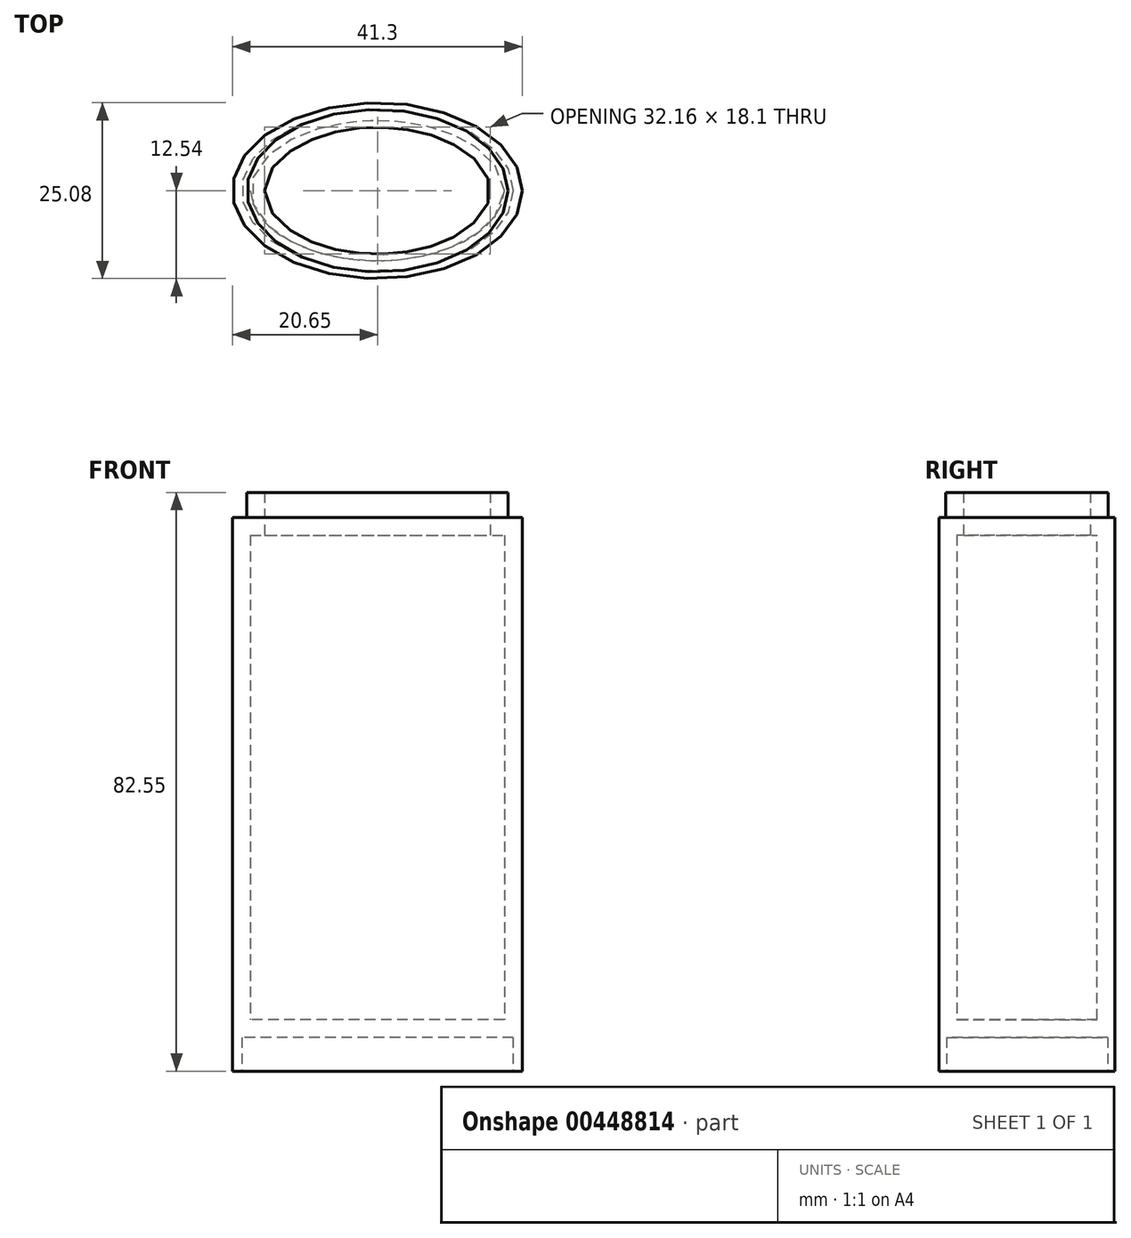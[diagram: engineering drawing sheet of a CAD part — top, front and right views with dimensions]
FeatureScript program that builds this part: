
annotation { "Feature Type Name" : "Feature", "Feature Type Description" : "" }
export const myFeature = defineFeature(function(context is Context, id is Id, definition is map)
    precondition{}
    {
        {
            var Q0;
            Q0=qCreatedBy(makeId("Top.planeOp"),FACE);
            var sketch = newSketch(context, id + "F0", { "sketchPlane" : qUnion([Q0])});
            skEllipse(sketch, "E0", {"center": v(0, 0) * mm, "majorRadius": 20.65 * mm, "minorRadius": 12.54 * mm, "majorAxis": v(1, 0)});
            skSolve(sketch);
        }
        {
            var Q0;
            Q0 = qSketchRegion(id + "F0", true);
            extrude(context, id + "F1", {"entities" : qUnion([Q0]), "depth" : 79 * mm});
        }
        {
            var Q0;
            Q0=makeQuery(id+"F1.opExtrude","CAP_FACE",FACE,{"disambiguationData":[OSD([sQuery(id+"F0.wireOp",EDGE,"E0")])],"isStart":true});
            var sketch = newSketch(context, id + "F2", { "sketchPlane" : qUnion([Q0])});
            skEllipse(sketch, "E1", {"center": v(0, 0) * mm, "majorRadius": 19.36 * mm, "minorRadius": 11.49 * mm, "majorAxis": v(1, 0)});
            skSolve(sketch);
        }
        {
            var Q0;
            Q0 = qSketchRegion(id + "F2", true);
            extrude(context, id + "F3", {"entities" : qUnion([Q0]), "operationType" : NewBodyOperationType.REMOVE, "oppositeDirection" : true, "depth" : 4.83 * mm});
        }
        {
            var Q0;
            Q0=makeQuery(id+"F1.opExtrude","CAP_FACE",FACE,{"disambiguationData":[OSD([sQuery(id+"F0.wireOp",EDGE,"E0")])],"isStart":false});
            var sketch = newSketch(context, id + "F4", { "sketchPlane" : qUnion([Q0])});
            skEllipse(sketch, "E2", {"center": v(0, 0) * mm, "majorRadius": 18.62 * mm, "minorRadius": 11.6 * mm, "majorAxis": v(1, 0)});
            skSolve(sketch);
        }
        {
            var Q0;
            Q0 = qSketchRegion(id + "F4", true);
            extrude(context, id + "F5", {"entities" : qUnion([Q0]), "operationType" : NewBodyOperationType.ADD, "depth" : 3.56 * mm});
        }
        {
            var Q0;
            Q0=makeQuery(id+"F5.opExtrude","CAP_FACE",FACE,{"disambiguationData":[OSD([sQuery(id+"F4.wireOp",EDGE,"E2")])],"isStart":false});
            shell(context, id + "F6", {"entities" : qUnion([Q0]), "thickness" : 2.54 * mm});
        }
    });
